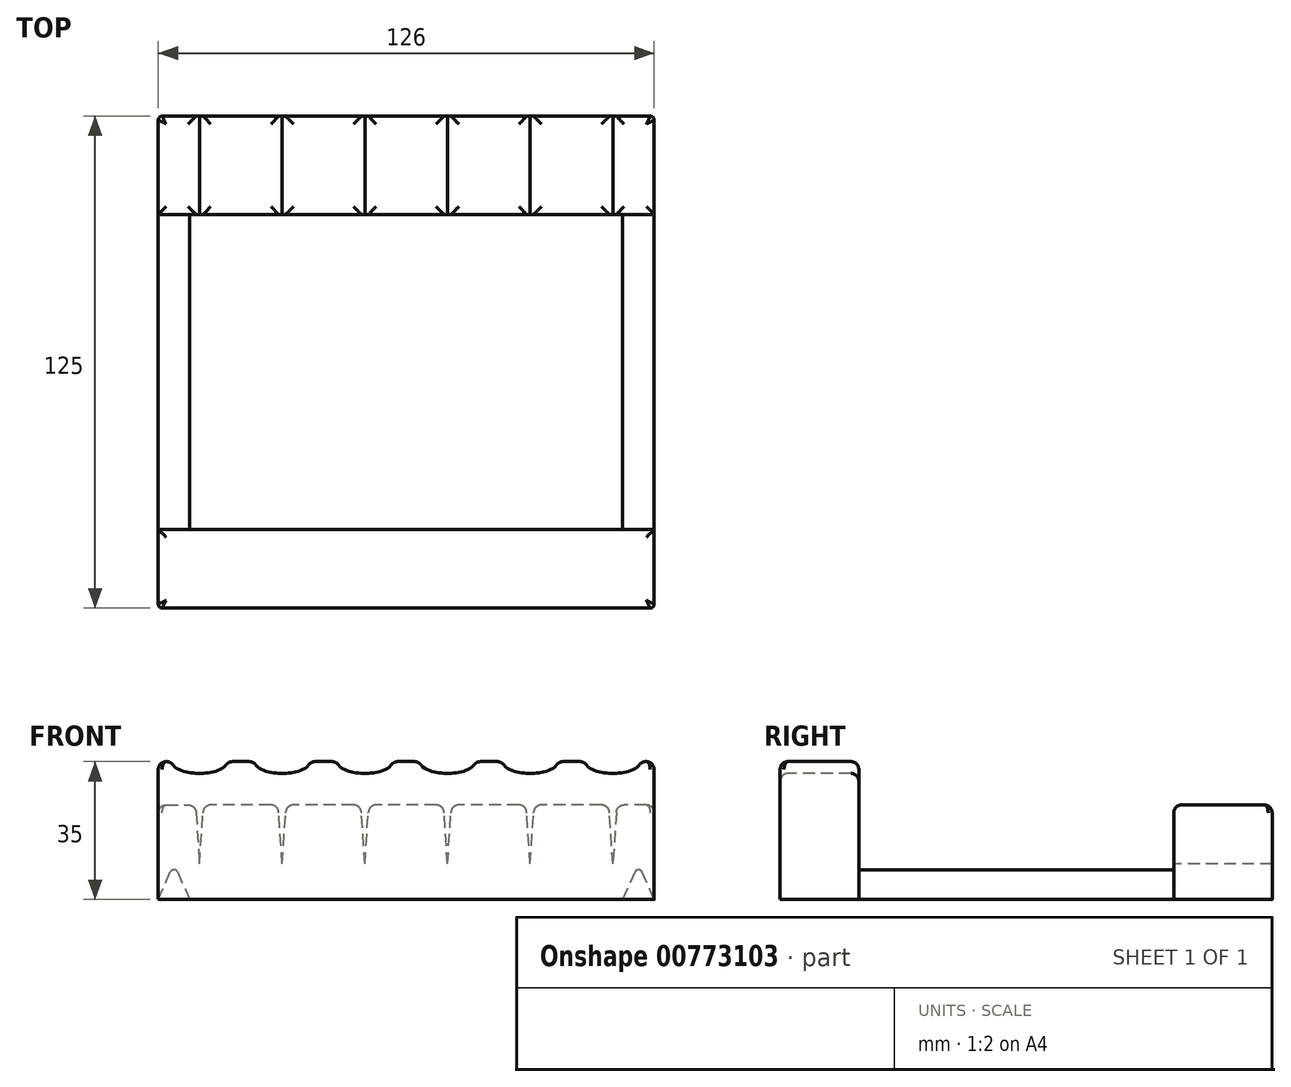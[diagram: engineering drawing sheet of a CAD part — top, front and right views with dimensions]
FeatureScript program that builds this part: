
annotation { "Feature Type Name" : "Feature", "Feature Type Description" : "" }
export const myFeature = defineFeature(function(context is Context, id is Id, definition is map)
    precondition{}
    {
        {
            var Q0;
            Q0=qCreatedBy(makeId("Front.planeOp"),FACE);
            var sketch = newSketch(context, id + "F0", { "sketchPlane" : qUnion([Q0])});
            skLineSegment(sketch, "E0.bottom", {"start": v(-63, 17.5) * mm, "end": v(63, 17.5) * mm});
            skLineSegment(sketch, "E0.top", {"start": v(-63, -17.5) * mm, "end": v(63, -17.5) * mm});
            skLineSegment(sketch, "E0.left", {"start": v(-63, 17.5) * mm, "end": v(-63, -17.5) * mm});
            skLineSegment(sketch, "E0.right", {"start": v(63, 17.5) * mm, "end": v(63, -17.5) * mm});
            skPoint(sketch, "E0.middle", {"position": v(0, 0) * mm});
            skPoint(sketch, "E1", {"position": v(0, 17.5) * mm});
            skLineSegment(sketch, "E2", {"start": v(-63, 6.5) * mm, "end": v(63, 6.5) * mm});
            skLineSegment(sketch, "E3", {"start": v(-63, -17.5) * mm, "end": v(-59, -8.5) * mm});
            skLineSegment(sketch, "E4", {"start": v(-59, -8.5) * mm, "end": v(-55, -17.5) * mm});
            skLineSegment(sketch, "E5", {"start": v(63, -17.5) * mm, "end": v(59, -8.5) * mm});
            skLineSegment(sketch, "E6", {"start": v(59, -8.5) * mm, "end": v(55, -17.5) * mm});
            skLineSegment(sketch, "E7", {"start": v(-63, -8.5) * mm, "end": v(63, -8.5) * mm});
            skLineSegment(sketch, "E8", {"start": v(-63, 17.5) * mm, "end": v(-63, -8.5) * mm});
            skLineSegment(sketch, "E9", {"start": v(-42, 17.5) * mm, "end": v(-42, -8.5) * mm});
            skLineSegment(sketch, "E10", {"start": v(-21, 17.5) * mm, "end": v(-21, -8.5) * mm});
            skLineSegment(sketch, "E11", {"start": v(0, 17.5) * mm, "end": v(0, -8.5) * mm});
            skLineSegment(sketch, "E12", {"start": v(21, 17.5) * mm, "end": v(21, -8.5) * mm});
            skLineSegment(sketch, "E13", {"start": v(42, 17.5) * mm, "end": v(42, -8.5) * mm});
            skEllipse(sketch, "E14", {"center": v(52.5, 17.5) * mm, "majorRadius": 7 * mm, "minorRadius": 3 * mm, "majorAxis": v(1, 0)});
            skEllipse(sketch, "E15", {"center": v(31.5, 17.5) * mm, "majorRadius": 7 * mm, "minorRadius": 3 * mm, "majorAxis": v(1, 0)});
            skEllipse(sketch, "E16", {"center": v(10.5, 17.5) * mm, "majorRadius": 7 * mm, "minorRadius": 3 * mm, "majorAxis": v(1, 0)});
            skEllipse(sketch, "E17", {"center": v(-10.5, 17.5) * mm, "majorRadius": 7 * mm, "minorRadius": 3 * mm, "majorAxis": v(1, 0)});
            skEllipse(sketch, "E18", {"center": v(-31.5, 17.5) * mm, "majorRadius": 7 * mm, "minorRadius": 3 * mm, "majorAxis": v(1, 0)});
            skEllipse(sketch, "E19", {"center": v(-52.5, 17.5) * mm, "majorRadius": 7 * mm, "minorRadius": 3 * mm, "majorAxis": v(1, 0)});
            skLineSegment(sketch, "E20", {"start": v(52.5, 17.5) * mm, "end": v(52.5, -8.5) * mm});
            skLineSegment(sketch, "E21", {"start": v(31.5, 17.5) * mm, "end": v(31.5, -8.5) * mm});
            skLineSegment(sketch, "E22", {"start": v(10.5, 17.5) * mm, "end": v(10.5, -8.5) * mm});
            skLineSegment(sketch, "E23", {"start": v(-10.5, 17.5) * mm, "end": v(-10.5, -8.5) * mm});
            skLineSegment(sketch, "E24", {"start": v(-31.5, 17.5) * mm, "end": v(-31.5, -8.5) * mm});
            skLineSegment(sketch, "E25", {"start": v(-52.5, 17.5) * mm, "end": v(-52.5, -8.5) * mm});
            skLineSegment(sketch, "E26", {"start": v(-53.5, 6.5) * mm, "end": v(-52.5, -8.5) * mm});
            skLineSegment(sketch, "E27", {"start": v(-51.5, 6.5) * mm, "end": v(-52.5, -8.5) * mm});
            skLineSegment(sketch, "E28", {"start": v(-32.5, 6.5) * mm, "end": v(-31.5, -8.5) * mm});
            skLineSegment(sketch, "E29", {"start": v(-30.5, 6.5) * mm, "end": v(-31.5, -8.5) * mm});
            skLineSegment(sketch, "E30", {"start": v(-11.5, 6.5) * mm, "end": v(-10.5, -8.5) * mm});
            skLineSegment(sketch, "E31", {"start": v(-9.5, 6.5) * mm, "end": v(-10.5, -8.5) * mm});
            skLineSegment(sketch, "E32", {"start": v(9.5, 6.5) * mm, "end": v(10.5, -8.5) * mm});
            skLineSegment(sketch, "E33", {"start": v(11.5, 6.5) * mm, "end": v(10.5, -8.5) * mm});
            skLineSegment(sketch, "E34", {"start": v(30.5, 6.5) * mm, "end": v(31.5, -8.5) * mm});
            skLineSegment(sketch, "E35", {"start": v(32.5, 6.5) * mm, "end": v(31.5, -8.5) * mm});
            skLineSegment(sketch, "E36", {"start": v(51.5, 6.5) * mm, "end": v(52.5, -8.5) * mm});
            skLineSegment(sketch, "E37", {"start": v(53.5, 6.5) * mm, "end": v(52.5, -8.5) * mm});
            skSolve(sketch);
        }
        {
            var Q0;
            {var subQ0=sQuery(id+"F0.wireOp",EDGE,"E3");Q0=makeQuery(id+"F0.imprint","IMPRINT",FACE,{"disambiguationData":[TD([[makeQuery(id+"F0.imprint","IMPRINT",EDGE,{"derivedFrom":subQ0}),1.0]])]});}
            var Q1;
            {var subQ11=sQuery(id+"F0.wireOp",EDGE,"E4");Q1=makeQuery(id+"F0.imprint","IMPRINT",FACE,{"disambiguationData":[TD([[makeQuery(id+"F0.imprint","IMPRINT",EDGE,{"derivedFrom":subQ11}),1.0]])]});}
            var Q2;
            {var subQ2=sQuery(id+"F0.wireOp",EDGE,"E3");Q2=makeQuery(id+"F0.imprint","IMPRINT",FACE,{"disambiguationData":[TD([[makeQuery(id+"F0.imprint","IMPRINT",EDGE,{"derivedFrom":subQ2}),-1.0]])]});}
            var Q3;
            {var subQ0=sQuery(id+"F0.wireOp",EDGE,"E5");Q3=makeQuery(id+"F0.imprint","IMPRINT",FACE,{"disambiguationData":[TD([[makeQuery(id+"F0.imprint","IMPRINT",EDGE,{"derivedFrom":subQ0}),-1.0]])]});}
            var Q4;
            {var subQ0=sQuery(id+"F0.wireOp",EDGE,"E5");Q4=makeQuery(id+"F0.imprint","IMPRINT",FACE,{"disambiguationData":[TD([[makeQuery(id+"F0.imprint","IMPRINT",EDGE,{"derivedFrom":subQ0}),1.0]])]});}
            var Q5;
            {var subQ2=sQuery(id+"F0.wireOp",EDGE,"E37");Q5=makeQuery(id+"F0.imprint","IMPRINT",FACE,{"disambiguationData":[TD([[makeQuery(id+"F0.imprint","IMPRINT",EDGE,{"derivedFrom":subQ2}),1.0]])]});}
            var Q6;
            {var subQ3=sQuery(id+"F0.wireOp",EDGE,"E36");Q6=makeQuery(id+"F0.imprint","IMPRINT",FACE,{"disambiguationData":[TD([[makeQuery(id+"F0.imprint","IMPRINT",EDGE,{"derivedFrom":subQ3}),-1.0]])]});}
            var Q7;
            {var subQ3=sQuery(id+"F0.wireOp",EDGE,"E35");Q7=makeQuery(id+"F0.imprint","IMPRINT",FACE,{"disambiguationData":[TD([[makeQuery(id+"F0.imprint","IMPRINT",EDGE,{"derivedFrom":subQ3}),1.0]])]});}
            var Q8;
            {var subQ3=sQuery(id+"F0.wireOp",EDGE,"E34");Q8=makeQuery(id+"F0.imprint","IMPRINT",FACE,{"disambiguationData":[TD([[makeQuery(id+"F0.imprint","IMPRINT",EDGE,{"derivedFrom":subQ3}),-1.0]])]});}
            var Q9;
            {var subQ3=sQuery(id+"F0.wireOp",EDGE,"E33");Q9=makeQuery(id+"F0.imprint","IMPRINT",FACE,{"disambiguationData":[TD([[makeQuery(id+"F0.imprint","IMPRINT",EDGE,{"derivedFrom":subQ3}),1.0]])]});}
            var Q10;
            {var subQ3=sQuery(id+"F0.wireOp",EDGE,"E32");Q10=makeQuery(id+"F0.imprint","IMPRINT",FACE,{"disambiguationData":[TD([[makeQuery(id+"F0.imprint","IMPRINT",EDGE,{"derivedFrom":subQ3}),-1.0]])]});}
            var Q11;
            {var subQ3=sQuery(id+"F0.wireOp",EDGE,"E31");Q11=makeQuery(id+"F0.imprint","IMPRINT",FACE,{"disambiguationData":[TD([[makeQuery(id+"F0.imprint","IMPRINT",EDGE,{"derivedFrom":subQ3}),1.0]])]});}
            var Q12;
            {var subQ3=sQuery(id+"F0.wireOp",EDGE,"E30");Q12=makeQuery(id+"F0.imprint","IMPRINT",FACE,{"disambiguationData":[TD([[makeQuery(id+"F0.imprint","IMPRINT",EDGE,{"derivedFrom":subQ3}),-1.0]])]});}
            var Q13;
            {var subQ3=sQuery(id+"F0.wireOp",EDGE,"E29");Q13=makeQuery(id+"F0.imprint","IMPRINT",FACE,{"disambiguationData":[TD([[makeQuery(id+"F0.imprint","IMPRINT",EDGE,{"derivedFrom":subQ3}),1.0]])]});}
            var Q14;
            {var subQ3=sQuery(id+"F0.wireOp",EDGE,"E28");Q14=makeQuery(id+"F0.imprint","IMPRINT",FACE,{"disambiguationData":[TD([[makeQuery(id+"F0.imprint","IMPRINT",EDGE,{"derivedFrom":subQ3}),-1.0]])]});}
            var Q15;
            {var subQ3=sQuery(id+"F0.wireOp",EDGE,"E27");Q15=makeQuery(id+"F0.imprint","IMPRINT",FACE,{"disambiguationData":[TD([[makeQuery(id+"F0.imprint","IMPRINT",EDGE,{"derivedFrom":subQ3}),1.0]])]});}
            var Q16;
            {var subQ6=sQuery(id+"F0.wireOp",EDGE,"E26");Q16=makeQuery(id+"F0.imprint","IMPRINT",FACE,{"disambiguationData":[TD([[makeQuery(id+"F0.imprint","IMPRINT",EDGE,{"derivedFrom":subQ6}),-1.0]])]});}
            var Q17;
            {var subQ3=sQuery(id+"F0.wireOp",EDGE,"E26");Q17=makeQuery(id+"F0.imprint","IMPRINT",FACE,{"disambiguationData":[TD([[makeQuery(id+"F0.imprint","IMPRINT",EDGE,{"derivedFrom":subQ3}),1.0]])]});}
            var Q18;
            {var subQ3=sQuery(id+"F0.wireOp",EDGE,"E27");Q18=makeQuery(id+"F0.imprint","IMPRINT",FACE,{"disambiguationData":[TD([[makeQuery(id+"F0.imprint","IMPRINT",EDGE,{"derivedFrom":subQ3}),-1.0]])]});}
            var Q19;
            {var subQ3=sQuery(id+"F0.wireOp",EDGE,"E28");Q19=makeQuery(id+"F0.imprint","IMPRINT",FACE,{"disambiguationData":[TD([[makeQuery(id+"F0.imprint","IMPRINT",EDGE,{"derivedFrom":subQ3}),1.0]])]});}
            var Q20;
            {var subQ3=sQuery(id+"F0.wireOp",EDGE,"E29");Q20=makeQuery(id+"F0.imprint","IMPRINT",FACE,{"disambiguationData":[TD([[makeQuery(id+"F0.imprint","IMPRINT",EDGE,{"derivedFrom":subQ3}),-1.0]])]});}
            var Q21;
            {var subQ3=sQuery(id+"F0.wireOp",EDGE,"E30");Q21=makeQuery(id+"F0.imprint","IMPRINT",FACE,{"disambiguationData":[TD([[makeQuery(id+"F0.imprint","IMPRINT",EDGE,{"derivedFrom":subQ3}),1.0]])]});}
            var Q22;
            {var subQ3=sQuery(id+"F0.wireOp",EDGE,"E31");Q22=makeQuery(id+"F0.imprint","IMPRINT",FACE,{"disambiguationData":[TD([[makeQuery(id+"F0.imprint","IMPRINT",EDGE,{"derivedFrom":subQ3}),-1.0]])]});}
            var Q23;
            {var subQ0=sQuery(id+"F0.wireOp",EDGE,"E37");Q23=makeQuery(id+"F0.imprint","IMPRINT",FACE,{"disambiguationData":[TD([[makeQuery(id+"F0.imprint","IMPRINT",EDGE,{"derivedFrom":subQ0}),-1.0]])]});}
            var Q24;
            {var subQ3=sQuery(id+"F0.wireOp",EDGE,"E36");Q24=makeQuery(id+"F0.imprint","IMPRINT",FACE,{"disambiguationData":[TD([[makeQuery(id+"F0.imprint","IMPRINT",EDGE,{"derivedFrom":subQ3}),1.0]])]});}
            var Q25;
            {var subQ3=sQuery(id+"F0.wireOp",EDGE,"E35");Q25=makeQuery(id+"F0.imprint","IMPRINT",FACE,{"disambiguationData":[TD([[makeQuery(id+"F0.imprint","IMPRINT",EDGE,{"derivedFrom":subQ3}),-1.0]])]});}
            var Q26;
            {var subQ3=sQuery(id+"F0.wireOp",EDGE,"E34");Q26=makeQuery(id+"F0.imprint","IMPRINT",FACE,{"disambiguationData":[TD([[makeQuery(id+"F0.imprint","IMPRINT",EDGE,{"derivedFrom":subQ3}),1.0]])]});}
            var Q27;
            {var subQ3=sQuery(id+"F0.wireOp",EDGE,"E33");Q27=makeQuery(id+"F0.imprint","IMPRINT",FACE,{"disambiguationData":[TD([[makeQuery(id+"F0.imprint","IMPRINT",EDGE,{"derivedFrom":subQ3}),-1.0]])]});}
            var Q28;
            {var subQ3=sQuery(id+"F0.wireOp",EDGE,"E32");Q28=makeQuery(id+"F0.imprint","IMPRINT",FACE,{"disambiguationData":[TD([[makeQuery(id+"F0.imprint","IMPRINT",EDGE,{"derivedFrom":subQ3}),1.0]])]});}
            var Q29;
            {var subQ1=sQuery(id+"F0.wireOp",EDGE,"E0.right");var subQ6=sQuery(id+"F0.wireOp",EDGE,"E0.bottom");var subQ7=makeQuery(id+"F0.imprint","INTERSECT",VERTEX,{"derivedFrom":[subQ6,subQ1]});Q29=makeQuery(id+"F0.imprint","IMPRINT",FACE,{"disambiguationData":[TD([[makeQuery(id+"F0.imprint","IMPRINT",EDGE,{"disambiguationData":[TD([[subQ7,1.0]])],"derivedFrom":subQ6}),-1.0]])]});}
            var Q30;
            {var subQ4=sQuery(id+"F0.wireOp",EDGE,"E13");var subQ6=sQuery(id+"F0.wireOp",EDGE,"E0.bottom");var subQ7=makeQuery(id+"F0.imprint","INTERSECT",VERTEX,{"derivedFrom":[subQ6,subQ4]});Q30=makeQuery(id+"F0.imprint","IMPRINT",FACE,{"disambiguationData":[TD([[makeQuery(id+"F0.imprint","IMPRINT",EDGE,{"disambiguationData":[TD([[subQ7,-1.0]])],"derivedFrom":subQ6}),-1.0]])]});}
            var Q31;
            {var subQ4=sQuery(id+"F0.wireOp",EDGE,"E13");var subQ6=sQuery(id+"F0.wireOp",EDGE,"E0.bottom");var subQ7=makeQuery(id+"F0.imprint","INTERSECT",VERTEX,{"derivedFrom":[subQ6,subQ4]});Q31=makeQuery(id+"F0.imprint","IMPRINT",FACE,{"disambiguationData":[TD([[makeQuery(id+"F0.imprint","IMPRINT",EDGE,{"disambiguationData":[TD([[subQ7,1.0]])],"derivedFrom":subQ6}),-1.0]])]});}
            var Q32;
            {var subQ0=sQuery(id+"F0.wireOp",EDGE,"E12");var subQ1=sQuery(id+"F0.wireOp",EDGE,"E0.bottom");var subQ2=makeQuery(id+"F0.imprint","INTERSECT",VERTEX,{"derivedFrom":[subQ1,subQ0]});Q32=makeQuery(id+"F0.imprint","IMPRINT",FACE,{"disambiguationData":[TD([[makeQuery(id+"F0.imprint","IMPRINT",EDGE,{"disambiguationData":[TD([[subQ2,-1.0]])],"derivedFrom":subQ1}),-1.0]])]});}
            var Q33;
            {var subQ0=sQuery(id+"F0.wireOp",EDGE,"E12");var subQ1=sQuery(id+"F0.wireOp",EDGE,"E0.bottom");var subQ2=makeQuery(id+"F0.imprint","INTERSECT",VERTEX,{"derivedFrom":[subQ1,subQ0]});Q33=makeQuery(id+"F0.imprint","IMPRINT",FACE,{"disambiguationData":[TD([[makeQuery(id+"F0.imprint","IMPRINT",EDGE,{"disambiguationData":[TD([[subQ2,1.0]])],"derivedFrom":subQ1}),-1.0]])]});}
            var Q34;
            {var subQ0=sQuery(id+"F0.wireOp",EDGE,"E11");var subQ3=sQuery(id+"F0.wireOp",EDGE,"E0.bottom");var subQ4=makeQuery(id+"F0.imprint","INTERSECT",VERTEX,{"derivedFrom":[subQ3,subQ0]});Q34=makeQuery(id+"F0.imprint","IMPRINT",FACE,{"disambiguationData":[TD([[makeQuery(id+"F0.imprint","IMPRINT",EDGE,{"disambiguationData":[TD([[subQ4,-1.0]])],"derivedFrom":subQ3}),-1.0]])]});}
            var Q35;
            {var subQ0=sQuery(id+"F0.wireOp",EDGE,"E11");var subQ7=sQuery(id+"F0.wireOp",EDGE,"E0.bottom");var subQ9=makeQuery(id+"F0.imprint","INTERSECT",VERTEX,{"derivedFrom":[subQ7,subQ0]});Q35=makeQuery(id+"F0.imprint","IMPRINT",FACE,{"disambiguationData":[TD([[makeQuery(id+"F0.imprint","IMPRINT",EDGE,{"disambiguationData":[TD([[subQ9,1.0]])],"derivedFrom":subQ7}),-1.0]])]});}
            var Q36;
            {var subQ0=sQuery(id+"F0.wireOp",EDGE,"E10");var subQ3=sQuery(id+"F0.wireOp",EDGE,"E0.bottom");var subQ4=makeQuery(id+"F0.imprint","INTERSECT",VERTEX,{"derivedFrom":[subQ3,subQ0]});Q36=makeQuery(id+"F0.imprint","IMPRINT",FACE,{"disambiguationData":[TD([[makeQuery(id+"F0.imprint","IMPRINT",EDGE,{"disambiguationData":[TD([[subQ4,-1.0]])],"derivedFrom":subQ3}),-1.0]])]});}
            var Q37;
            {var subQ0=sQuery(id+"F0.wireOp",EDGE,"E10");var subQ3=sQuery(id+"F0.wireOp",EDGE,"E0.bottom");var subQ4=makeQuery(id+"F0.imprint","INTERSECT",VERTEX,{"derivedFrom":[subQ3,subQ0]});Q37=makeQuery(id+"F0.imprint","IMPRINT",FACE,{"disambiguationData":[TD([[makeQuery(id+"F0.imprint","IMPRINT",EDGE,{"disambiguationData":[TD([[subQ4,1.0]])],"derivedFrom":subQ3}),-1.0]])]});}
            var Q38;
            {var subQ0=sQuery(id+"F0.wireOp",EDGE,"E9");var subQ3=sQuery(id+"F0.wireOp",EDGE,"E0.bottom");var subQ4=makeQuery(id+"F0.imprint","INTERSECT",VERTEX,{"derivedFrom":[subQ3,subQ0]});Q38=makeQuery(id+"F0.imprint","IMPRINT",FACE,{"disambiguationData":[TD([[makeQuery(id+"F0.imprint","IMPRINT",EDGE,{"disambiguationData":[TD([[subQ4,-1.0]])],"derivedFrom":subQ3}),-1.0]])]});}
            var Q39;
            {var subQ0=sQuery(id+"F0.wireOp",EDGE,"E9");var subQ3=sQuery(id+"F0.wireOp",EDGE,"E0.bottom");var subQ4=makeQuery(id+"F0.imprint","INTERSECT",VERTEX,{"derivedFrom":[subQ3,subQ0]});Q39=makeQuery(id+"F0.imprint","IMPRINT",FACE,{"disambiguationData":[TD([[makeQuery(id+"F0.imprint","IMPRINT",EDGE,{"disambiguationData":[TD([[subQ4,1.0]])],"derivedFrom":subQ3}),-1.0]])]});}
            var Q40;
            {var subQ4=sQuery(id+"F0.wireOp",EDGE,"E19");var subQ8=sQuery(id+"F0.wireOp",EDGE,"E0.bottom");var subQ10=makeQuery(id+"F0.imprint","INTERSECT",VERTEX,{"disambiguationData":[OD(0.0)],"derivedFrom":[subQ8,subQ4]});Q40=makeQuery(id+"F0.imprint","IMPRINT",FACE,{"disambiguationData":[TD([[makeQuery(id+"F0.imprint","IMPRINT",EDGE,{"disambiguationData":[TD([[subQ10,1.0]])],"derivedFrom":subQ8}),-1.0]])]});}
            extrude(context, id + "F1", {"entities" : qUnion([Q0, Q1, Q2, Q3, Q4, Q5, Q6, Q7, Q8, Q9, Q10, Q11, Q12, Q13, Q14, Q15, Q16, Q17, Q18, Q19, Q20, Q21, Q22, Q23, Q24, Q25, Q26, Q27, Q28, Q29, Q30, Q31, Q32, Q33, Q34, Q35, Q36, Q37, Q38, Q39, Q40]), "depth" : 60 * mm, "offsetDistance" : 25 * mm});
        }
        {
            var Q0;
            {var subQ2=sQuery(id+"F0.wireOp",EDGE,"E37");Q0=makeQuery(id+"F0.imprint","IMPRINT",FACE,{"disambiguationData":[TD([[makeQuery(id+"F0.imprint","IMPRINT",EDGE,{"derivedFrom":subQ2}),1.0]])]});}
            var Q1;
            {var subQ3=sQuery(id+"F0.wireOp",EDGE,"E36");Q1=makeQuery(id+"F0.imprint","IMPRINT",FACE,{"disambiguationData":[TD([[makeQuery(id+"F0.imprint","IMPRINT",EDGE,{"derivedFrom":subQ3}),-1.0]])]});}
            var Q2;
            {var subQ3=sQuery(id+"F0.wireOp",EDGE,"E35");Q2=makeQuery(id+"F0.imprint","IMPRINT",FACE,{"disambiguationData":[TD([[makeQuery(id+"F0.imprint","IMPRINT",EDGE,{"derivedFrom":subQ3}),1.0]])]});}
            var Q3;
            {var subQ3=sQuery(id+"F0.wireOp",EDGE,"E34");Q3=makeQuery(id+"F0.imprint","IMPRINT",FACE,{"disambiguationData":[TD([[makeQuery(id+"F0.imprint","IMPRINT",EDGE,{"derivedFrom":subQ3}),-1.0]])]});}
            var Q4;
            {var subQ3=sQuery(id+"F0.wireOp",EDGE,"E33");Q4=makeQuery(id+"F0.imprint","IMPRINT",FACE,{"disambiguationData":[TD([[makeQuery(id+"F0.imprint","IMPRINT",EDGE,{"derivedFrom":subQ3}),1.0]])]});}
            var Q5;
            {var subQ3=sQuery(id+"F0.wireOp",EDGE,"E32");Q5=makeQuery(id+"F0.imprint","IMPRINT",FACE,{"disambiguationData":[TD([[makeQuery(id+"F0.imprint","IMPRINT",EDGE,{"derivedFrom":subQ3}),-1.0]])]});}
            var Q6;
            {var subQ3=sQuery(id+"F0.wireOp",EDGE,"E31");Q6=makeQuery(id+"F0.imprint","IMPRINT",FACE,{"disambiguationData":[TD([[makeQuery(id+"F0.imprint","IMPRINT",EDGE,{"derivedFrom":subQ3}),1.0]])]});}
            var Q7;
            {var subQ3=sQuery(id+"F0.wireOp",EDGE,"E30");Q7=makeQuery(id+"F0.imprint","IMPRINT",FACE,{"disambiguationData":[TD([[makeQuery(id+"F0.imprint","IMPRINT",EDGE,{"derivedFrom":subQ3}),-1.0]])]});}
            var Q8;
            {var subQ3=sQuery(id+"F0.wireOp",EDGE,"E28");Q8=makeQuery(id+"F0.imprint","IMPRINT",FACE,{"disambiguationData":[TD([[makeQuery(id+"F0.imprint","IMPRINT",EDGE,{"derivedFrom":subQ3}),-1.0]])]});}
            var Q9;
            {var subQ3=sQuery(id+"F0.wireOp",EDGE,"E27");Q9=makeQuery(id+"F0.imprint","IMPRINT",FACE,{"disambiguationData":[TD([[makeQuery(id+"F0.imprint","IMPRINT",EDGE,{"derivedFrom":subQ3}),1.0]])]});}
            var Q10;
            {var subQ6=sQuery(id+"F0.wireOp",EDGE,"E26");Q10=makeQuery(id+"F0.imprint","IMPRINT",FACE,{"disambiguationData":[TD([[makeQuery(id+"F0.imprint","IMPRINT",EDGE,{"derivedFrom":subQ6}),-1.0]])]});}
            var Q11;
            {var subQ3=sQuery(id+"F0.wireOp",EDGE,"E29");Q11=makeQuery(id+"F0.imprint","IMPRINT",FACE,{"disambiguationData":[TD([[makeQuery(id+"F0.imprint","IMPRINT",EDGE,{"derivedFrom":subQ3}),1.0]])]});}
            var Q12;
            {var subQ0=sQuery(id+"F0.wireOp",EDGE,"E3");Q12=makeQuery(id+"F0.imprint","IMPRINT",FACE,{"disambiguationData":[TD([[makeQuery(id+"F0.imprint","IMPRINT",EDGE,{"derivedFrom":subQ0}),1.0]])]});}
            var Q13;
            {var subQ2=sQuery(id+"F0.wireOp",EDGE,"E3");Q13=makeQuery(id+"F0.imprint","IMPRINT",FACE,{"disambiguationData":[TD([[makeQuery(id+"F0.imprint","IMPRINT",EDGE,{"derivedFrom":subQ2}),-1.0]])]});}
            var Q14;
            {var subQ11=sQuery(id+"F0.wireOp",EDGE,"E4");Q14=makeQuery(id+"F0.imprint","IMPRINT",FACE,{"disambiguationData":[TD([[makeQuery(id+"F0.imprint","IMPRINT",EDGE,{"derivedFrom":subQ11}),1.0]])]});}
            var Q15;
            {var subQ0=sQuery(id+"F0.wireOp",EDGE,"E5");Q15=makeQuery(id+"F0.imprint","IMPRINT",FACE,{"disambiguationData":[TD([[makeQuery(id+"F0.imprint","IMPRINT",EDGE,{"derivedFrom":subQ0}),1.0]])]});}
            var Q16;
            {var subQ0=sQuery(id+"F0.wireOp",EDGE,"E5");Q16=makeQuery(id+"F0.imprint","IMPRINT",FACE,{"disambiguationData":[TD([[makeQuery(id+"F0.imprint","IMPRINT",EDGE,{"derivedFrom":subQ0}),-1.0]])]});}
            extrude(context, id + "F2", {"entities" : qUnion([Q0, Q1, Q2, Q3, Q4, Q5, Q6, Q7, Q8, Q9, Q10, Q11, Q12, Q13, Q14, Q15, Q16]), "operationType" : NewBodyOperationType.ADD, "oppositeDirection" : true, "depth" : 65 * mm, "offsetDistance" : 25 * mm});
        }
        {
            var Q0;
            {var subQ3=sQuery(id+"F0.wireOp",EDGE,"E36");Q0=makeQuery(id+"F0.imprint","IMPRINT",FACE,{"disambiguationData":[TD([[makeQuery(id+"F0.imprint","IMPRINT",EDGE,{"derivedFrom":subQ3}),-1.0]])]});}
            var Q1;
            {var subQ3=sQuery(id+"F0.wireOp",EDGE,"E29");Q1=makeQuery(id+"F0.imprint","IMPRINT",FACE,{"disambiguationData":[TD([[makeQuery(id+"F0.imprint","IMPRINT",EDGE,{"derivedFrom":subQ3}),-1.0]])]});}
            var Q2;
            {var subQ3=sQuery(id+"F0.wireOp",EDGE,"E29");Q2=makeQuery(id+"F0.imprint","IMPRINT",FACE,{"disambiguationData":[TD([[makeQuery(id+"F0.imprint","IMPRINT",EDGE,{"derivedFrom":subQ3}),1.0]])]});}
            var Q3;
            {var subQ3=sQuery(id+"F0.wireOp",EDGE,"E28");Q3=makeQuery(id+"F0.imprint","IMPRINT",FACE,{"disambiguationData":[TD([[makeQuery(id+"F0.imprint","IMPRINT",EDGE,{"derivedFrom":subQ3}),-1.0]])]});}
            var Q4;
            {var subQ0=sQuery(id+"F0.wireOp",EDGE,"E3");Q4=makeQuery(id+"F0.imprint","IMPRINT",FACE,{"disambiguationData":[TD([[makeQuery(id+"F0.imprint","IMPRINT",EDGE,{"derivedFrom":subQ0}),1.0]])]});}
            var Q5;
            {var subQ2=sQuery(id+"F0.wireOp",EDGE,"E37");Q5=makeQuery(id+"F0.imprint","IMPRINT",FACE,{"disambiguationData":[TD([[makeQuery(id+"F0.imprint","IMPRINT",EDGE,{"derivedFrom":subQ2}),1.0]])]});}
            var Q6;
            {var subQ3=sQuery(id+"F0.wireOp",EDGE,"E34");Q6=makeQuery(id+"F0.imprint","IMPRINT",FACE,{"disambiguationData":[TD([[makeQuery(id+"F0.imprint","IMPRINT",EDGE,{"derivedFrom":subQ3}),-1.0]])]});}
            var Q7;
            {var subQ3=sQuery(id+"F0.wireOp",EDGE,"E30");Q7=makeQuery(id+"F0.imprint","IMPRINT",FACE,{"disambiguationData":[TD([[makeQuery(id+"F0.imprint","IMPRINT",EDGE,{"derivedFrom":subQ3}),1.0]])]});}
            var Q8;
            {var subQ3=sQuery(id+"F0.wireOp",EDGE,"E30");Q8=makeQuery(id+"F0.imprint","IMPRINT",FACE,{"disambiguationData":[TD([[makeQuery(id+"F0.imprint","IMPRINT",EDGE,{"derivedFrom":subQ3}),-1.0]])]});}
            var Q9;
            {var subQ3=sQuery(id+"F0.wireOp",EDGE,"E28");Q9=makeQuery(id+"F0.imprint","IMPRINT",FACE,{"disambiguationData":[TD([[makeQuery(id+"F0.imprint","IMPRINT",EDGE,{"derivedFrom":subQ3}),1.0]])]});}
            var Q10;
            {var subQ0=sQuery(id+"F0.wireOp",EDGE,"E37");Q10=makeQuery(id+"F0.imprint","IMPRINT",FACE,{"disambiguationData":[TD([[makeQuery(id+"F0.imprint","IMPRINT",EDGE,{"derivedFrom":subQ0}),-1.0]])]});}
            var Q11;
            {var subQ0=sQuery(id+"F0.wireOp",EDGE,"E5");Q11=makeQuery(id+"F0.imprint","IMPRINT",FACE,{"disambiguationData":[TD([[makeQuery(id+"F0.imprint","IMPRINT",EDGE,{"derivedFrom":subQ0}),-1.0]])]});}
            var Q12;
            {var subQ3=sQuery(id+"F0.wireOp",EDGE,"E36");Q12=makeQuery(id+"F0.imprint","IMPRINT",FACE,{"disambiguationData":[TD([[makeQuery(id+"F0.imprint","IMPRINT",EDGE,{"derivedFrom":subQ3}),1.0]])]});}
            var Q13;
            {var subQ3=sQuery(id+"F0.wireOp",EDGE,"E26");Q13=makeQuery(id+"F0.imprint","IMPRINT",FACE,{"disambiguationData":[TD([[makeQuery(id+"F0.imprint","IMPRINT",EDGE,{"derivedFrom":subQ3}),1.0]])]});}
            var Q14;
            {var subQ3=sQuery(id+"F0.wireOp",EDGE,"E27");Q14=makeQuery(id+"F0.imprint","IMPRINT",FACE,{"disambiguationData":[TD([[makeQuery(id+"F0.imprint","IMPRINT",EDGE,{"derivedFrom":subQ3}),1.0]])]});}
            var Q15;
            {var subQ3=sQuery(id+"F0.wireOp",EDGE,"E33");Q15=makeQuery(id+"F0.imprint","IMPRINT",FACE,{"disambiguationData":[TD([[makeQuery(id+"F0.imprint","IMPRINT",EDGE,{"derivedFrom":subQ3}),1.0]])]});}
            var Q16;
            {var subQ3=sQuery(id+"F0.wireOp",EDGE,"E34");Q16=makeQuery(id+"F0.imprint","IMPRINT",FACE,{"disambiguationData":[TD([[makeQuery(id+"F0.imprint","IMPRINT",EDGE,{"derivedFrom":subQ3}),1.0]])]});}
            var Q17;
            {var subQ6=sQuery(id+"F0.wireOp",EDGE,"E26");Q17=makeQuery(id+"F0.imprint","IMPRINT",FACE,{"disambiguationData":[TD([[makeQuery(id+"F0.imprint","IMPRINT",EDGE,{"derivedFrom":subQ6}),-1.0]])]});}
            var Q18;
            {var subQ3=sQuery(id+"F0.wireOp",EDGE,"E35");Q18=makeQuery(id+"F0.imprint","IMPRINT",FACE,{"disambiguationData":[TD([[makeQuery(id+"F0.imprint","IMPRINT",EDGE,{"derivedFrom":subQ3}),1.0]])]});}
            var Q19;
            {var subQ3=sQuery(id+"F0.wireOp",EDGE,"E32");Q19=makeQuery(id+"F0.imprint","IMPRINT",FACE,{"disambiguationData":[TD([[makeQuery(id+"F0.imprint","IMPRINT",EDGE,{"derivedFrom":subQ3}),-1.0]])]});}
            var Q20;
            {var subQ3=sQuery(id+"F0.wireOp",EDGE,"E33");Q20=makeQuery(id+"F0.imprint","IMPRINT",FACE,{"disambiguationData":[TD([[makeQuery(id+"F0.imprint","IMPRINT",EDGE,{"derivedFrom":subQ3}),-1.0]])]});}
            var Q21;
            {var subQ3=sQuery(id+"F0.wireOp",EDGE,"E31");Q21=makeQuery(id+"F0.imprint","IMPRINT",FACE,{"disambiguationData":[TD([[makeQuery(id+"F0.imprint","IMPRINT",EDGE,{"derivedFrom":subQ3}),1.0]])]});}
            var Q22;
            {var subQ11=sQuery(id+"F0.wireOp",EDGE,"E4");Q22=makeQuery(id+"F0.imprint","IMPRINT",FACE,{"disambiguationData":[TD([[makeQuery(id+"F0.imprint","IMPRINT",EDGE,{"derivedFrom":subQ11}),1.0]])]});}
            var Q23;
            {var subQ3=sQuery(id+"F0.wireOp",EDGE,"E35");Q23=makeQuery(id+"F0.imprint","IMPRINT",FACE,{"disambiguationData":[TD([[makeQuery(id+"F0.imprint","IMPRINT",EDGE,{"derivedFrom":subQ3}),-1.0]])]});}
            var Q24;
            {var subQ3=sQuery(id+"F0.wireOp",EDGE,"E31");Q24=makeQuery(id+"F0.imprint","IMPRINT",FACE,{"disambiguationData":[TD([[makeQuery(id+"F0.imprint","IMPRINT",EDGE,{"derivedFrom":subQ3}),-1.0]])]});}
            var Q25;
            {var subQ3=sQuery(id+"F0.wireOp",EDGE,"E27");Q25=makeQuery(id+"F0.imprint","IMPRINT",FACE,{"disambiguationData":[TD([[makeQuery(id+"F0.imprint","IMPRINT",EDGE,{"derivedFrom":subQ3}),-1.0]])]});}
            var Q26;
            {var subQ3=sQuery(id+"F0.wireOp",EDGE,"E32");Q26=makeQuery(id+"F0.imprint","IMPRINT",FACE,{"disambiguationData":[TD([[makeQuery(id+"F0.imprint","IMPRINT",EDGE,{"derivedFrom":subQ3}),1.0]])]});}
            var Q27;
            {var subQ4=sQuery(id+"F0.wireOp",EDGE,"E19");var subQ8=sQuery(id+"F0.wireOp",EDGE,"E0.bottom");var subQ10=makeQuery(id+"F0.imprint","INTERSECT",VERTEX,{"disambiguationData":[OD(0.0)],"derivedFrom":[subQ8,subQ4]});Q27=makeQuery(id+"F0.imprint","IMPRINT",FACE,{"disambiguationData":[TD([[makeQuery(id+"F0.imprint","IMPRINT",EDGE,{"disambiguationData":[TD([[subQ10,1.0]])],"derivedFrom":subQ8}),-1.0]])]});}
            var Q28;
            {var subQ0=sQuery(id+"F0.wireOp",EDGE,"E9");var subQ3=sQuery(id+"F0.wireOp",EDGE,"E0.bottom");var subQ4=makeQuery(id+"F0.imprint","INTERSECT",VERTEX,{"derivedFrom":[subQ3,subQ0]});Q28=makeQuery(id+"F0.imprint","IMPRINT",FACE,{"disambiguationData":[TD([[makeQuery(id+"F0.imprint","IMPRINT",EDGE,{"disambiguationData":[TD([[subQ4,1.0]])],"derivedFrom":subQ3}),-1.0]])]});}
            var Q29;
            {var subQ0=sQuery(id+"F0.wireOp",EDGE,"E9");var subQ3=sQuery(id+"F0.wireOp",EDGE,"E0.bottom");var subQ4=makeQuery(id+"F0.imprint","INTERSECT",VERTEX,{"derivedFrom":[subQ3,subQ0]});Q29=makeQuery(id+"F0.imprint","IMPRINT",FACE,{"disambiguationData":[TD([[makeQuery(id+"F0.imprint","IMPRINT",EDGE,{"disambiguationData":[TD([[subQ4,-1.0]])],"derivedFrom":subQ3}),-1.0]])]});}
            var Q30;
            {var subQ0=sQuery(id+"F0.wireOp",EDGE,"E10");var subQ3=sQuery(id+"F0.wireOp",EDGE,"E0.bottom");var subQ4=makeQuery(id+"F0.imprint","INTERSECT",VERTEX,{"derivedFrom":[subQ3,subQ0]});Q30=makeQuery(id+"F0.imprint","IMPRINT",FACE,{"disambiguationData":[TD([[makeQuery(id+"F0.imprint","IMPRINT",EDGE,{"disambiguationData":[TD([[subQ4,1.0]])],"derivedFrom":subQ3}),-1.0]])]});}
            var Q31;
            {var subQ0=sQuery(id+"F0.wireOp",EDGE,"E10");var subQ3=sQuery(id+"F0.wireOp",EDGE,"E0.bottom");var subQ4=makeQuery(id+"F0.imprint","INTERSECT",VERTEX,{"derivedFrom":[subQ3,subQ0]});Q31=makeQuery(id+"F0.imprint","IMPRINT",FACE,{"disambiguationData":[TD([[makeQuery(id+"F0.imprint","IMPRINT",EDGE,{"disambiguationData":[TD([[subQ4,-1.0]])],"derivedFrom":subQ3}),-1.0]])]});}
            var Q32;
            {var subQ0=sQuery(id+"F0.wireOp",EDGE,"E11");var subQ7=sQuery(id+"F0.wireOp",EDGE,"E0.bottom");var subQ9=makeQuery(id+"F0.imprint","INTERSECT",VERTEX,{"derivedFrom":[subQ7,subQ0]});Q32=makeQuery(id+"F0.imprint","IMPRINT",FACE,{"disambiguationData":[TD([[makeQuery(id+"F0.imprint","IMPRINT",EDGE,{"disambiguationData":[TD([[subQ9,1.0]])],"derivedFrom":subQ7}),-1.0]])]});}
            var Q33;
            {var subQ0=sQuery(id+"F0.wireOp",EDGE,"E11");var subQ3=sQuery(id+"F0.wireOp",EDGE,"E0.bottom");var subQ4=makeQuery(id+"F0.imprint","INTERSECT",VERTEX,{"derivedFrom":[subQ3,subQ0]});Q33=makeQuery(id+"F0.imprint","IMPRINT",FACE,{"disambiguationData":[TD([[makeQuery(id+"F0.imprint","IMPRINT",EDGE,{"disambiguationData":[TD([[subQ4,-1.0]])],"derivedFrom":subQ3}),-1.0]])]});}
            var Q34;
            {var subQ0=sQuery(id+"F0.wireOp",EDGE,"E12");var subQ1=sQuery(id+"F0.wireOp",EDGE,"E0.bottom");var subQ2=makeQuery(id+"F0.imprint","INTERSECT",VERTEX,{"derivedFrom":[subQ1,subQ0]});Q34=makeQuery(id+"F0.imprint","IMPRINT",FACE,{"disambiguationData":[TD([[makeQuery(id+"F0.imprint","IMPRINT",EDGE,{"disambiguationData":[TD([[subQ2,1.0]])],"derivedFrom":subQ1}),-1.0]])]});}
            var Q35;
            {var subQ0=sQuery(id+"F0.wireOp",EDGE,"E12");var subQ1=sQuery(id+"F0.wireOp",EDGE,"E0.bottom");var subQ2=makeQuery(id+"F0.imprint","INTERSECT",VERTEX,{"derivedFrom":[subQ1,subQ0]});Q35=makeQuery(id+"F0.imprint","IMPRINT",FACE,{"disambiguationData":[TD([[makeQuery(id+"F0.imprint","IMPRINT",EDGE,{"disambiguationData":[TD([[subQ2,-1.0]])],"derivedFrom":subQ1}),-1.0]])]});}
            var Q36;
            {var subQ4=sQuery(id+"F0.wireOp",EDGE,"E13");var subQ6=sQuery(id+"F0.wireOp",EDGE,"E0.bottom");var subQ7=makeQuery(id+"F0.imprint","INTERSECT",VERTEX,{"derivedFrom":[subQ6,subQ4]});Q36=makeQuery(id+"F0.imprint","IMPRINT",FACE,{"disambiguationData":[TD([[makeQuery(id+"F0.imprint","IMPRINT",EDGE,{"disambiguationData":[TD([[subQ7,1.0]])],"derivedFrom":subQ6}),-1.0]])]});}
            var Q37;
            {var subQ4=sQuery(id+"F0.wireOp",EDGE,"E13");var subQ6=sQuery(id+"F0.wireOp",EDGE,"E0.bottom");var subQ7=makeQuery(id+"F0.imprint","INTERSECT",VERTEX,{"derivedFrom":[subQ6,subQ4]});Q37=makeQuery(id+"F0.imprint","IMPRINT",FACE,{"disambiguationData":[TD([[makeQuery(id+"F0.imprint","IMPRINT",EDGE,{"disambiguationData":[TD([[subQ7,-1.0]])],"derivedFrom":subQ6}),-1.0]])]});}
            var Q38;
            {var subQ1=sQuery(id+"F0.wireOp",EDGE,"E0.right");var subQ6=sQuery(id+"F0.wireOp",EDGE,"E0.bottom");var subQ7=makeQuery(id+"F0.imprint","INTERSECT",VERTEX,{"derivedFrom":[subQ6,subQ1]});Q38=makeQuery(id+"F0.imprint","IMPRINT",FACE,{"disambiguationData":[TD([[makeQuery(id+"F0.imprint","IMPRINT",EDGE,{"disambiguationData":[TD([[subQ7,1.0]])],"derivedFrom":subQ6}),-1.0]])]});}
            extrude(context, id + "F3", {"entities" : qUnion([Q0, Q1, Q2, Q3, Q4, Q5, Q6, Q7, Q8, Q9, Q10, Q11, Q12, Q13, Q14, Q15, Q16, Q17, Q18, Q19, Q20, Q21, Q22, Q23, Q24, Q25, Q26, Q27, Q28, Q29, Q30, Q31, Q32, Q33, Q34, Q35, Q36, Q37, Q38]), "operationType" : NewBodyOperationType.REMOVE, "oppositeDirection" : true, "depth" : 80 * mm, "offsetDistance" : 25 * mm, "symmetric" : true});
        }
        {
            var Q0;
            Q0=makeQuery(id+"F3.boolean.opBoolean","COPY",EDGE,{"derivedFrom":makeQuery(id+"F3.opExtrude","SWEPT_EDGE",EDGE,{"disambiguationData":[OSD([sQuery(id+"F0.wireOp",EDGE,"E3"),sQuery(id+"F0.wireOp",EDGE,"E4"),sQuery(id+"F0.wireOp",EDGE,"E7")])]})});
            var Q1;
            Q1=makeQuery(id+"F3.boolean.opBoolean","COPY",EDGE,{"derivedFrom":makeQuery(id+"F3.opExtrude","SWEPT_EDGE",EDGE,{"disambiguationData":[OSD([sQuery(id+"F0.wireOp",EDGE,"E5"),sQuery(id+"F0.wireOp",EDGE,"E6"),sQuery(id+"F0.wireOp",EDGE,"E7")])]})});
            var Q2;
            Q2=makeQuery(id+"F2.opExtrude","CAP_EDGE",EDGE,{"disambiguationData":[OSD([sQuery(id+"F0.wireOp",EDGE,"E0.left")])],"isStart":false});
            var Q3;
            Q3=makeQuery(id+"F1.opExtrude","CAP_EDGE",EDGE,{"disambiguationData":[OSD([sQuery(id+"F0.wireOp",EDGE,"E0.left")])],"isStart":false});
            var Q4;
            Q4=makeQuery(id+"F3.boolean.opBoolean","COPY",EDGE,{"derivedFrom":makeQuery(id+"F3.opExtrude","CAP_EDGE",EDGE,{"disambiguationData":[OSD([sQuery(id+"F0.wireOp",EDGE,"E0.left")])],"isStart":true})});
            var Q5;
            Q5=makeQuery(id+"F3.boolean.opBoolean","COPY",EDGE,{"derivedFrom":makeQuery(id+"F3.opExtrude","CAP_EDGE",EDGE,{"disambiguationData":[OSD([sQuery(id+"F0.wireOp",EDGE,"E0.left")])],"isStart":false})});
            var Q6;
            Q6=makeQuery(id+"F2.opExtrude","CAP_EDGE",EDGE,{"disambiguationData":[OSD([sQuery(id+"F0.wireOp",EDGE,"E0.right")])],"isStart":false});
            var Q7;
            Q7=makeQuery(id+"F3.boolean.opBoolean","COPY",EDGE,{"derivedFrom":makeQuery(id+"F3.opExtrude","CAP_EDGE",EDGE,{"disambiguationData":[OSD([sQuery(id+"F0.wireOp",EDGE,"E0.right")])],"isStart":false})});
            var Q8;
            Q8=makeQuery(id+"F3.boolean.opBoolean","COPY",EDGE,{"derivedFrom":makeQuery(id+"F3.opExtrude","CAP_EDGE",EDGE,{"disambiguationData":[OSD([sQuery(id+"F0.wireOp",EDGE,"E0.right")])],"isStart":true})});
            var Q9;
            Q9=makeQuery(id+"F1.opExtrude","CAP_EDGE",EDGE,{"disambiguationData":[OSD([sQuery(id+"F0.wireOp",EDGE,"E0.right")])],"isStart":false});
            fillet(context, id + "F4", {"entities" : qUnion([Q0, Q1, Q2, Q3, Q4, Q5, Q6, Q7, Q8, Q9]), "radius" : 1 * mm, "tangentPropagation" : true, "allowEdgeOverflow" : false});
        }
        {
            var Q0;
            {var subQ0=sQuery(id+"F0.wireOp",EDGE,"E0.bottom");Q0=makeQuery(id+"F1.opExtrude","SWEPT_FACE",FACE,{"disambiguationData":[OSD([subQ0]),TDD([makeQuery(id+"F0.imprint","IMPRINT",EDGE,{"disambiguationData":[TD([[makeQuery(id+"F0.imprint","INTERSECT",VERTEX,{"derivedFrom":[subQ0,sQuery(id+"F0.wireOp",EDGE,"E0.right")]}),1.0]])],"derivedFrom":subQ0})])]});}
            var Q1;
            {var subQ0=sQuery(id+"F0.wireOp",EDGE,"E0.bottom");var subQ1=makeQuery(id+"F0.imprint","INTERSECT",VERTEX,{"derivedFrom":[subQ0,sQuery(id+"F0.wireOp",EDGE,"E13")]});Q1=makeQuery(id+"F1.opExtrude","SWEPT_FACE",FACE,{"disambiguationData":[OSD([subQ0]),TDD([makeQuery(id+"F0.imprint","IMPRINT",EDGE,{"disambiguationData":[TD([[subQ1,-1.0]])],"derivedFrom":subQ0}),makeQuery(id+"F0.imprint","IMPRINT",EDGE,{"disambiguationData":[TD([[subQ1,1.0]])],"derivedFrom":subQ0})])]});}
            var Q2;
            {var subQ0=sQuery(id+"F0.wireOp",EDGE,"E0.bottom");var subQ1=makeQuery(id+"F0.imprint","INTERSECT",VERTEX,{"derivedFrom":[subQ0,sQuery(id+"F0.wireOp",EDGE,"E12")]});Q2=makeQuery(id+"F1.opExtrude","SWEPT_FACE",FACE,{"disambiguationData":[OSD([subQ0]),TDD([makeQuery(id+"F0.imprint","IMPRINT",EDGE,{"disambiguationData":[TD([[subQ1,-1.0]])],"derivedFrom":subQ0}),makeQuery(id+"F0.imprint","IMPRINT",EDGE,{"disambiguationData":[TD([[subQ1,1.0]])],"derivedFrom":subQ0})])]});}
            var Q3;
            {var subQ0=sQuery(id+"F0.wireOp",EDGE,"E0.bottom");var subQ1=makeQuery(id+"F0.imprint","INTERSECT",VERTEX,{"derivedFrom":[subQ0,sQuery(id+"F0.wireOp",EDGE,"E11")]});Q3=makeQuery(id+"F1.opExtrude","SWEPT_FACE",FACE,{"disambiguationData":[OSD([subQ0]),TDD([makeQuery(id+"F0.imprint","IMPRINT",EDGE,{"disambiguationData":[TD([[subQ1,-1.0]])],"derivedFrom":subQ0}),makeQuery(id+"F0.imprint","IMPRINT",EDGE,{"disambiguationData":[TD([[subQ1,1.0]])],"derivedFrom":subQ0})])]});}
            var Q4;
            {var subQ0=sQuery(id+"F0.wireOp",EDGE,"E0.bottom");var subQ1=makeQuery(id+"F0.imprint","INTERSECT",VERTEX,{"derivedFrom":[subQ0,sQuery(id+"F0.wireOp",EDGE,"E10")]});Q4=makeQuery(id+"F1.opExtrude","SWEPT_FACE",FACE,{"disambiguationData":[OSD([subQ0]),TDD([makeQuery(id+"F0.imprint","IMPRINT",EDGE,{"disambiguationData":[TD([[subQ1,-1.0]])],"derivedFrom":subQ0}),makeQuery(id+"F0.imprint","IMPRINT",EDGE,{"disambiguationData":[TD([[subQ1,1.0]])],"derivedFrom":subQ0})])]});}
            var Q5;
            {var subQ0=sQuery(id+"F0.wireOp",EDGE,"E19");var subQ1=sQuery(id+"F0.wireOp",EDGE,"E0.bottom");Q5=makeQuery(id+"F1.opExtrude","SWEPT_EDGE",EDGE,{"disambiguationData":[OSD([subQ1,subQ0]),TDD([makeQuery(id+"F0.imprint","INTERSECT",VERTEX,{"disambiguationData":[OD(1.0)],"derivedFrom":[subQ1,subQ0]})])]});}
            var Q6;
            {var subQ0=sQuery(id+"F0.wireOp",EDGE,"E0.bottom");var subQ1=makeQuery(id+"F0.imprint","INTERSECT",VERTEX,{"derivedFrom":[subQ0,sQuery(id+"F0.wireOp",EDGE,"E9")]});Q6=makeQuery(id+"F1.opExtrude","SWEPT_FACE",FACE,{"disambiguationData":[OSD([subQ0]),TDD([makeQuery(id+"F0.imprint","IMPRINT",EDGE,{"disambiguationData":[TD([[subQ1,1.0]])],"derivedFrom":subQ0}),makeQuery(id+"F0.imprint","IMPRINT",EDGE,{"disambiguationData":[TD([[subQ1,-1.0]])],"derivedFrom":subQ0})])]});}
            var Q7;
            {var subQ0=sQuery(id+"F0.wireOp",EDGE,"E0.bottom");Q7=makeQuery(id+"F1.opExtrude","SWEPT_FACE",FACE,{"disambiguationData":[OSD([subQ0]),TDD([makeQuery(id+"F0.imprint","IMPRINT",EDGE,{"disambiguationData":[TD([[makeQuery(id+"F0.imprint","INTERSECT",VERTEX,{"disambiguationData":[OD(0.0)],"derivedFrom":[subQ0,sQuery(id+"F0.wireOp",EDGE,"E19")]}),1.0]])],"derivedFrom":subQ0})])]});}
            var Q8;
            {var subQ0=sQuery(id+"F0.wireOp",EDGE,"E2");Q8=makeQuery(id+"F2.opExtrude","SWEPT_FACE",FACE,{"disambiguationData":[OSD([subQ0]),TDD([makeQuery(id+"F0.imprint","IMPRINT",EDGE,{"disambiguationData":[TD([[makeQuery(id+"F0.imprint","INTERSECT",VERTEX,{"derivedFrom":[sQuery(id+"F0.wireOp",EDGE,"E0.left"),subQ0]}),-1.0]])],"derivedFrom":subQ0})])]});}
            var Q9;
            {var subQ0=sQuery(id+"F0.wireOp",EDGE,"E2");var subQ1=makeQuery(id+"F0.imprint","INTERSECT",VERTEX,{"derivedFrom":[subQ0,sQuery(id+"F0.wireOp",EDGE,"E9")]});Q9=makeQuery(id+"F2.opExtrude","SWEPT_FACE",FACE,{"disambiguationData":[OSD([subQ0]),TDD([makeQuery(id+"F0.imprint","IMPRINT",EDGE,{"disambiguationData":[TD([[subQ1,-1.0]])],"derivedFrom":subQ0}),makeQuery(id+"F0.imprint","IMPRINT",EDGE,{"disambiguationData":[TD([[subQ1,1.0]])],"derivedFrom":subQ0})])]});}
            var Q10;
            {var subQ0=sQuery(id+"F0.wireOp",EDGE,"E2");var subQ1=makeQuery(id+"F0.imprint","INTERSECT",VERTEX,{"derivedFrom":[subQ0,sQuery(id+"F0.wireOp",EDGE,"E10")]});Q10=makeQuery(id+"F2.opExtrude","SWEPT_FACE",FACE,{"disambiguationData":[OSD([subQ0]),TDD([makeQuery(id+"F0.imprint","IMPRINT",EDGE,{"disambiguationData":[TD([[subQ1,-1.0]])],"derivedFrom":subQ0}),makeQuery(id+"F0.imprint","IMPRINT",EDGE,{"disambiguationData":[TD([[subQ1,1.0]])],"derivedFrom":subQ0})])]});}
            var Q11;
            {var subQ0=sQuery(id+"F0.wireOp",EDGE,"E2");var subQ1=makeQuery(id+"F0.imprint","INTERSECT",VERTEX,{"derivedFrom":[subQ0,sQuery(id+"F0.wireOp",EDGE,"E11")]});Q11=makeQuery(id+"F2.opExtrude","SWEPT_FACE",FACE,{"disambiguationData":[OSD([subQ0]),TDD([makeQuery(id+"F0.imprint","IMPRINT",EDGE,{"disambiguationData":[TD([[subQ1,-1.0]])],"derivedFrom":subQ0}),makeQuery(id+"F0.imprint","IMPRINT",EDGE,{"disambiguationData":[TD([[subQ1,1.0]])],"derivedFrom":subQ0})])]});}
            var Q12;
            {var subQ0=sQuery(id+"F0.wireOp",EDGE,"E2");var subQ1=makeQuery(id+"F0.imprint","INTERSECT",VERTEX,{"derivedFrom":[subQ0,sQuery(id+"F0.wireOp",EDGE,"E12")]});Q12=makeQuery(id+"F2.opExtrude","SWEPT_FACE",FACE,{"disambiguationData":[OSD([subQ0]),TDD([makeQuery(id+"F0.imprint","IMPRINT",EDGE,{"disambiguationData":[TD([[subQ1,-1.0]])],"derivedFrom":subQ0}),makeQuery(id+"F0.imprint","IMPRINT",EDGE,{"disambiguationData":[TD([[subQ1,1.0]])],"derivedFrom":subQ0})])]});}
            var Q13;
            {var subQ0=sQuery(id+"F0.wireOp",EDGE,"E2");var subQ1=makeQuery(id+"F0.imprint","INTERSECT",VERTEX,{"derivedFrom":[subQ0,sQuery(id+"F0.wireOp",EDGE,"E13")]});Q13=makeQuery(id+"F2.opExtrude","SWEPT_FACE",FACE,{"disambiguationData":[OSD([subQ0]),TDD([makeQuery(id+"F0.imprint","IMPRINT",EDGE,{"disambiguationData":[TD([[subQ1,-1.0]])],"derivedFrom":subQ0}),makeQuery(id+"F0.imprint","IMPRINT",EDGE,{"disambiguationData":[TD([[subQ1,1.0]])],"derivedFrom":subQ0})])]});}
            var Q14;
            {var subQ0=sQuery(id+"F0.wireOp",EDGE,"E2");Q14=makeQuery(id+"F2.opExtrude","SWEPT_FACE",FACE,{"disambiguationData":[OSD([subQ0]),TDD([makeQuery(id+"F0.imprint","IMPRINT",EDGE,{"disambiguationData":[TD([[makeQuery(id+"F0.imprint","INTERSECT",VERTEX,{"derivedFrom":[sQuery(id+"F0.wireOp",EDGE,"E0.right"),subQ0]}),1.0]])],"derivedFrom":subQ0})])]});}
            var Q15;
            Q15=makeQuery(id+"F1.opExtrude","SWEPT_FACE",FACE,{"disambiguationData":[OSD([sQuery(id+"F0.wireOp",EDGE,"E19")])]});
            var Q16;
            Q16=makeQuery(id+"F1.opExtrude","SWEPT_FACE",FACE,{"disambiguationData":[OSD([sQuery(id+"F0.wireOp",EDGE,"E18")])]});
            var Q17;
            Q17=makeQuery(id+"F1.opExtrude","SWEPT_FACE",FACE,{"disambiguationData":[OSD([sQuery(id+"F0.wireOp",EDGE,"E17")])]});
            var Q18;
            Q18=makeQuery(id+"F1.opExtrude","SWEPT_FACE",FACE,{"disambiguationData":[OSD([sQuery(id+"F0.wireOp",EDGE,"E16")])]});
            var Q19;
            Q19=makeQuery(id+"F1.opExtrude","SWEPT_FACE",FACE,{"disambiguationData":[OSD([sQuery(id+"F0.wireOp",EDGE,"E15")])]});
            var Q20;
            Q20=makeQuery(id+"F1.opExtrude","SWEPT_FACE",FACE,{"disambiguationData":[OSD([sQuery(id+"F0.wireOp",EDGE,"E14")])]});
            fillet(context, id + "F5", {"entities" : qUnion([Q0, Q1, Q2, Q3, Q4, Q5, Q6, Q7, Q8, Q9, Q10, Q11, Q12, Q13, Q14, Q15, Q16, Q17, Q18, Q19, Q20]), "radius" : 2 * mm, "tangentPropagation" : true, "allowEdgeOverflow" : false});
        }
    });
